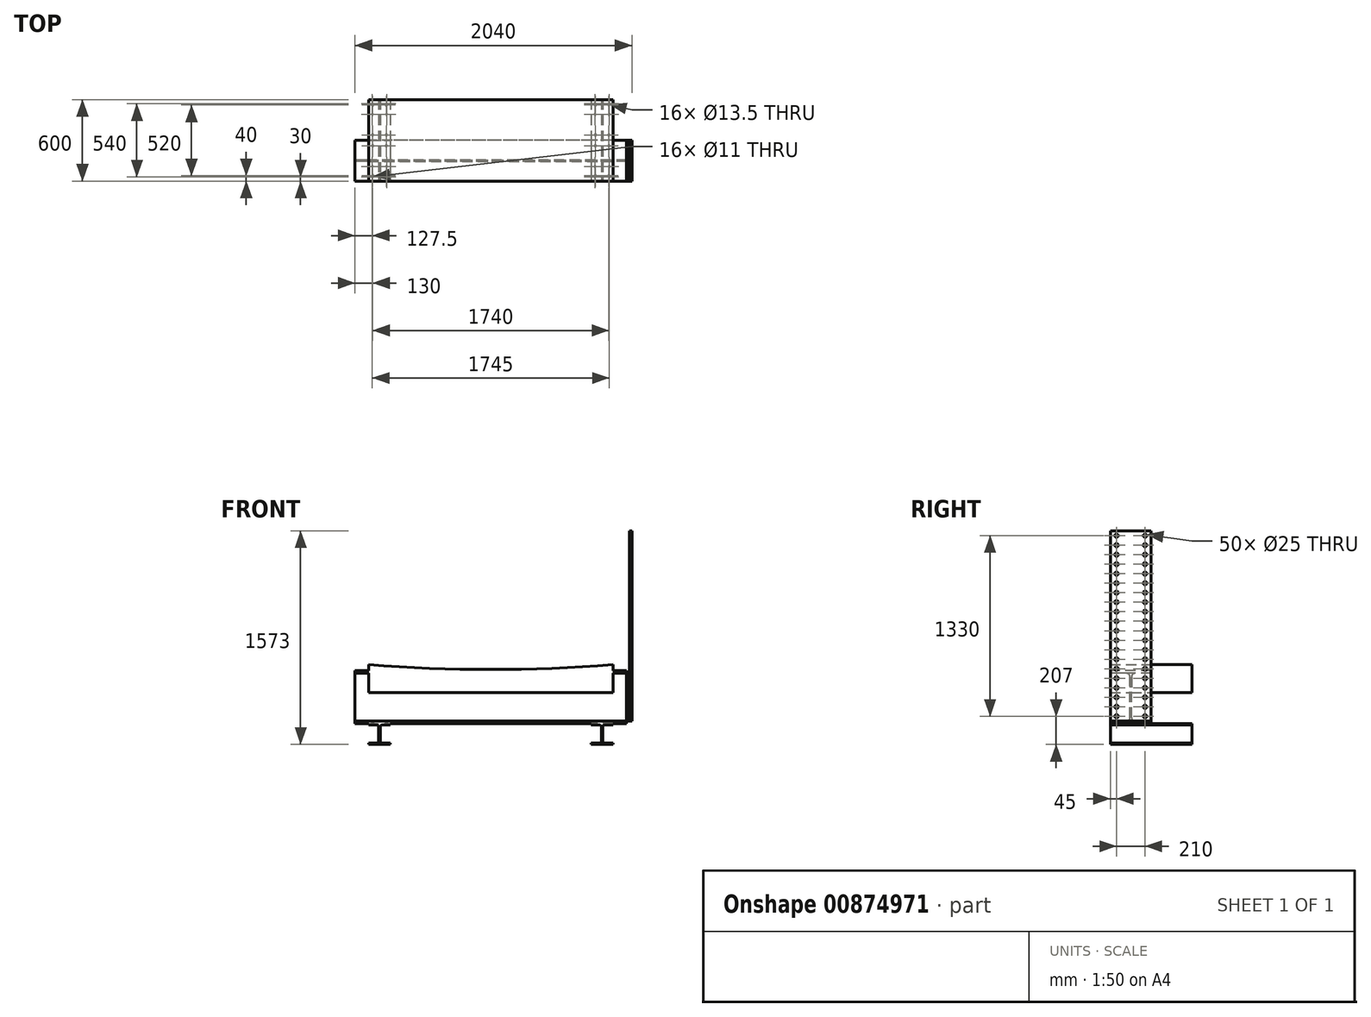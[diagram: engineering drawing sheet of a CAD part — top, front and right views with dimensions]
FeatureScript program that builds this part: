
annotation { "Feature Type Name" : "Feature", "Feature Type Description" : "" }
export const myFeature = defineFeature(function(context is Context, id is Id, definition is map)
    precondition{}
    {
        {
            var Q0;
            Q0=qCreatedBy(makeId("Front.planeOp"),FACE);
            var sketch = newSketch(context, id + "F0", { "sketchPlane" : qUnion([Q0])});
            skArc(sketch, "E0", {"start": v(-900, 40) * mm, "mid": v(0, 0) * mm, "end": v(900, 40) * mm});
            skLineSegment(sketch, "E1", {"start": v(-900, 40) * mm, "end": v(900, 40) * mm, "construction": true});
            skLineSegment(sketch, "E2", {"start": v(-900, 40) * mm, "end": v(-900, -160) * mm});
            skLineSegment(sketch, "E3", {"start": v(-900, -160) * mm, "end": v(900, -160) * mm});
            skLineSegment(sketch, "E4", {"start": v(900, -160) * mm, "end": v(900, 40) * mm});
            skSolve(sketch);
        }
        {
            var Q0;
            Q0=makeQuery(id+"F0.imprint","IMPRINT",FACE,{"disambiguationData":[TD([[makeQuery(id+"F0.imprint","IMPRINT",EDGE,{"derivedFrom":sQuery(id+"F0.wireOp",EDGE,"E0")}),-1.0]])]});
            extrude(context, id + "F1", {"entities" : qUnion([Q0]), "depth" : 300 * mm, "offsetDistance" : 25 * mm, "hasSecondDirection" : true, "secondDirectionOppositeDirection" : true, "secondDirectionDepth" : 300 * mm});
        }
        {
            var Q0;
            Q0=qCreatedBy(makeId("Front.planeOp"),FACE);
            var sketch = newSketch(context, id + "F2", { "sketchPlane" : qUnion([Q0])});
            skArc(sketch, "E5.0", {"start": v(-900, 40) * mm, "mid": v(0, 0) * mm, "end": v(900, 40) * mm});
            skLineSegment(sketch, "E6", {"start": v(-900, 40) * mm, "end": v(-900, 45) * mm});
            skLineSegment(sketch, "E7", {"start": v(900, 40) * mm, "end": v(900, 45) * mm});
            skArc(sketch, "E8", {"start": v(-900, 45) * mm, "mid": v(0, 10) * mm, "end": v(900, 45) * mm});
            skLineSegment(sketch, "E9", {"start": v(-900, 45) * mm, "end": v(900, 45) * mm, "construction": true});
            skSolve(sketch);
        }
        {
            var Q0;
            Q0 = qSketchRegion(id + "F2", true);
            extrude(context, id + "F3", {"entities" : qUnion([Q0]), "depth" : 300 * mm, "offsetDistance" : 25 * mm, "hasSecondDirection" : true, "secondDirectionOppositeDirection" : true, "secondDirectionDepth" : 300 * mm});
        }
        {
            var Q0;
            Q0=qCreatedBy(makeId("Right.planeOp"),FACE);
            var sketch = newSketch(context, id + "F4", { "sketchPlane" : qUnion([Q0])});
            skLineSegment(sketch, "E10", {"start": v(-150, 0) * mm, "end": v(0, 0) * mm});
            skLineSegment(sketch, "E11", {"start": v(0, 0) * mm, "end": v(0, -19) * mm});
            skLineSegment(sketch, "E12", {"start": v(0, -19) * mm, "end": v(-117.5, -19) * mm});
            skLineSegment(sketch, "E13", {"start": v(-144.5, -46) * mm, "end": v(-144.5, -195) * mm});
            skLineSegment(sketch, "E14", {"start": v(-144.5, -195) * mm, "end": v(-150, -195) * mm, "construction": true});
            skLineSegment(sketch, "E15", {"start": v(-150, -195) * mm, "end": v(-150, 0) * mm, "construction": true});
            skPoint(sketch, "E16.visualSharp", {"position": v(-144.5, -19) * mm});
            skArc(sketch, "E16.filletArc", {"start": v(-117.5, -19) * mm, "mid": v(-136.6, -26.9) * mm, "end": v(-144.5, -46) * mm});
            skLineSegment(sketch, "E17.MirrorCS", {"start": v(-150, 0) * mm, "end": v(-300, 0) * mm});
            skLineSegment(sketch, "E18.MirrorCS", {"start": v(-300, 0) * mm, "end": v(-300, -19) * mm});
            skLineSegment(sketch, "E19.MirrorCS", {"start": v(-300, -19) * mm, "end": v(-182.5, -19) * mm});
            skArc(sketch, "E20.MirrorCS", {"start": v(-182.5, -19) * mm, "mid": v(-163.4, -26.9) * mm, "end": v(-155.5, -46) * mm});
            skLineSegment(sketch, "E21.MirrorCS", {"start": v(-155.5, -46) * mm, "end": v(-155.5, -195) * mm});
            skLineSegment(sketch, "E22.MirrorCS", {"start": v(-144.5, -344) * mm, "end": v(-144.5, -195) * mm});
            skLineSegment(sketch, "E23.MirrorCS", {"start": v(0, -371) * mm, "end": v(-117.5, -371) * mm});
            skLineSegment(sketch, "E24.MirrorCS", {"start": v(0, -390) * mm, "end": v(0, -371) * mm});
            skLineSegment(sketch, "E25.MirrorCS", {"start": v(-150, -390) * mm, "end": v(0, -390) * mm});
            skLineSegment(sketch, "E26.MirrorCS", {"start": v(-150, -390) * mm, "end": v(-300, -390) * mm});
            skLineSegment(sketch, "E27.MirrorCS", {"start": v(-300, -390) * mm, "end": v(-300, -371) * mm});
            skLineSegment(sketch, "E28.MirrorCS", {"start": v(-300, -371) * mm, "end": v(-182.5, -371) * mm});
            skArc(sketch, "E29.MirrorCS", {"start": v(-182.5, -371) * mm, "mid": v(-163.4, -363.1) * mm, "end": v(-155.5, -344) * mm});
            skLineSegment(sketch, "E30.MirrorCS", {"start": v(-155.5, -344) * mm, "end": v(-155.5, -195) * mm});
            skArc(sketch, "E31.MirrorCS", {"start": v(-117.5, -371) * mm, "mid": v(-136.6, -363.1) * mm, "end": v(-144.5, -344) * mm});
            skSolve(sketch);
        }
        {
            var Q0;
            Q0=makeQuery(id+"F4.imprint","IMPRINT",FACE,{"disambiguationData":[TD([[makeQuery(id+"F4.imprint","IMPRINT",EDGE,{"derivedFrom":sQuery(id+"F4.wireOp",EDGE,"E10")}),-1.0]])]});
            extrude(context, id + "F5", {"entities" : qUnion([Q0]), "depth" : 1000 * mm, "offsetDistance" : 25 * mm, "hasSecondDirection" : true, "secondDirectionOppositeDirection" : true, "secondDirectionDepth" : 0 * mm});
        }
        {
            var Q0;
            Q0=makeQuery(id+"F5.opExtrude","CAP_FACE",FACE,{"disambiguationData":[OSD([sQuery(id+"F4.wireOp",EDGE,"E10"),sQuery(id+"F4.wireOp",EDGE,"E11"),sQuery(id+"F4.wireOp",EDGE,"E12"),sQuery(id+"F4.wireOp",EDGE,"E13"),sQuery(id+"F4.wireOp",EDGE,"E16.filletArc"),sQuery(id+"F4.wireOp",EDGE,"E17.MirrorCS"),sQuery(id+"F4.wireOp",EDGE,"E18.MirrorCS"),sQuery(id+"F4.wireOp",EDGE,"E19.MirrorCS"),sQuery(id+"F4.wireOp",EDGE,"E20.MirrorCS"),sQuery(id+"F4.wireOp",EDGE,"E21.MirrorCS"),sQuery(id+"F4.wireOp",EDGE,"E22.MirrorCS"),sQuery(id+"F4.wireOp",EDGE,"E23.MirrorCS"),sQuery(id+"F4.wireOp",EDGE,"E24.MirrorCS"),sQuery(id+"F4.wireOp",EDGE,"E25.MirrorCS"),sQuery(id+"F4.wireOp",EDGE,"E26.MirrorCS"),sQuery(id+"F4.wireOp",EDGE,"E27.MirrorCS"),sQuery(id+"F4.wireOp",EDGE,"E28.MirrorCS"),sQuery(id+"F4.wireOp",EDGE,"E29.MirrorCS"),sQuery(id+"F4.wireOp",EDGE,"E30.MirrorCS"),sQuery(id+"F4.wireOp",EDGE,"E31.MirrorCS")])],"isStart":false});
            var sketch = newSketch(context, id + "F6", { "sketchPlane" : qUnion([Q0])});
            skLineSegment(sketch, "E32.bottom", {"start": v(-300, -19) * mm, "end": v(0, -19) * mm});
            skLineSegment(sketch, "E32.top", {"start": v(-300, -371) * mm, "end": v(0, -371) * mm});
            skLineSegment(sketch, "E32.left", {"start": v(-300, -19) * mm, "end": v(-300, -371) * mm});
            skLineSegment(sketch, "E32.right", {"start": v(0, -19) * mm, "end": v(0, -371) * mm});
            skSolve(sketch);
        }
        {
            var Q0;
            Q0 = qSketchRegion(id + "F6", true);
            extrude(context, id + "F7", {"entities" : qUnion([Q0]), "depth" : 20 * mm, "offsetDistance" : 25 * mm});
        }
        {
            var Q0;
            Q0=makeQuery(id+"F7.opExtrude","CAP_FACE",FACE,{"disambiguationData":[OSD([sQuery(id+"F6.wireOp",EDGE,"E32.bottom"),sQuery(id+"F6.wireOp",EDGE,"E32.top"),sQuery(id+"F6.wireOp",EDGE,"E32.left"),sQuery(id+"F6.wireOp",EDGE,"E32.right")])],"isStart":false});
            var sketch = newSketch(context, id + "F8", { "sketchPlane" : qUnion([Q0])});
            skPoint(sketch, "E33", {"position": v(-255, -55) * mm});
            skPoint(sketch, "E34", {"position": v(-45, -55) * mm});
            skPoint(sketch, "E35", {"position": v(-45, -125) * mm});
            skPoint(sketch, "E36", {"position": v(-45, -195) * mm});
            skPoint(sketch, "E37", {"position": v(-45, -265) * mm});
            skPoint(sketch, "E38", {"position": v(-255, -125) * mm});
            skPoint(sketch, "E39", {"position": v(-255, -195) * mm});
            skPoint(sketch, "E40", {"position": v(-255, -265) * mm});
            skLineSegment(sketch, "E41", {"start": v(-150, -19) * mm, "end": v(-150, -371) * mm, "construction": true});
            skLineSegment(sketch, "E42", {"start": v(-255, -55) * mm, "end": v(-45, -55) * mm, "construction": true});
            skPoint(sketch, "E43", {"position": v(-150, -55) * mm});
            skLineSegment(sketch, "E44", {"start": v(-45, -55) * mm, "end": v(-45, -125) * mm, "construction": true});
            skLineSegment(sketch, "E45", {"start": v(-45, -195) * mm, "end": v(-45, -265) * mm, "construction": true});
            skLineSegment(sketch, "E46", {"start": v(-45, -195) * mm, "end": v(-45, -125) * mm, "construction": true});
            skPoint(sketch, "E47", {"position": v(-45, -335) * mm});
            skPoint(sketch, "E48", {"position": v(-255, -335) * mm});
            skLineSegment(sketch, "E49", {"start": v(-45, -265) * mm, "end": v(-45, -335) * mm, "construction": true});
            skLineSegment(sketch, "E50", {"start": v(-255, -55) * mm, "end": v(-255, -19) * mm, "construction": true});
            skLineSegment(sketch, "E51", {"start": v(-255, -335) * mm, "end": v(-255, -371) * mm, "construction": true});
            skCircle(sketch, "E52", {"center": v(-255, -55) * mm, "radius": 22 * mm, "construction": true});
            skCircle(sketch, "E53", {"center": v(-255, -125) * mm, "radius": 22 * mm, "construction": true});
            skSolve(sketch);
        }
        {
            var Q0;
            Q0=sQuery(id+"F8.wireOp",VERTEX,"E33");
            var Q1;
            Q1=sQuery(id+"F8.wireOp",VERTEX,"E34");
            var Q2;
            Q2=sQuery(id+"F8.wireOp",VERTEX,"E35");
            var Q3;
            Q3=sQuery(id+"F8.wireOp",VERTEX,"E38");
            var Q4;
            Q4=sQuery(id+"F8.wireOp",VERTEX,"E39");
            var Q5;
            Q5=sQuery(id+"F8.wireOp",VERTEX,"E36");
            var Q6;
            Q6=sQuery(id+"F8.wireOp",VERTEX,"E37");
            var Q7;
            Q7=sQuery(id+"F8.wireOp",VERTEX,"E47");
            var Q8;
            Q8=sQuery(id+"F8.wireOp",VERTEX,"E40");
            var Q9;
            Q9=sQuery(id+"F8.wireOp",VERTEX,"E48");
            var Q10;
            Q10=makeQuery(id+"F7.opExtrude","SWEPT_BODY",BODY,{"disambiguationData":[OSD([sQuery(id+"F6.wireOp",EDGE,"E32.bottom"),sQuery(id+"F6.wireOp",EDGE,"E32.top"),sQuery(id+"F6.wireOp",EDGE,"E32.left"),sQuery(id+"F6.wireOp",EDGE,"E32.right")])]});
            hole(context, id + "F9", {"style" : HoleStyle.SIMPLE, "endStyle" : HoleEndStyle.THROUGH, "holeDiameter" : 25 * mm, "majorDiameter" : 5 * mm, "isTappedThrough" : true, "tappedDepth" : 12 * mm, "tapClearance" : 3, "locations" : qUnion([Q0, Q1, Q2, Q3, Q4, Q5, Q6, Q7, Q8, Q9]), "scope" : qUnion([Q10])});
        }
        {
            var Q0;
            Q0=makeQuery(id+"F7.opExtrude","CAP_FACE",FACE,{"disambiguationData":[OSD([sQuery(id+"F6.wireOp",EDGE,"E32.bottom"),sQuery(id+"F6.wireOp",EDGE,"E32.top"),sQuery(id+"F6.wireOp",EDGE,"E32.left"),sQuery(id+"F6.wireOp",EDGE,"E32.right")])],"isStart":false});
            var sketch = newSketch(context, id + "F10", { "sketchPlane" : qUnion([Q0])});
            skLineSegment(sketch, "E54.bottom", {"start": v(-300, 1031) * mm, "end": v(0, 1031) * mm});
            skLineSegment(sketch, "E54.top", {"start": v(-300, -371) * mm, "end": v(0, -371) * mm});
            skLineSegment(sketch, "E54.left", {"start": v(-300, 1031) * mm, "end": v(-300, -371) * mm});
            skLineSegment(sketch, "E54.right", {"start": v(0, 1031) * mm, "end": v(0, -371) * mm});
            skPoint(sketch, "E55", {"position": v(-45, -335) * mm});
            skPoint(sketch, "E56", {"position": v(-255, -335) * mm});
            skPoint(sketch, "E57.0.1.0", {"position": v(-45, -265) * mm});
            skPoint(sketch, "E57.0.2.0", {"position": v(-45, -195) * mm});
            skPoint(sketch, "E57.0.3.0", {"position": v(-45, -125) * mm});
            skPoint(sketch, "E57.0.4.0", {"position": v(-45, -55) * mm});
            skPoint(sketch, "E57.0.5.0", {"position": v(-45, 15) * mm});
            skPoint(sketch, "E57.0.6.0", {"position": v(-45, 85) * mm});
            skPoint(sketch, "E57.0.7.0", {"position": v(-45, 155) * mm});
            skPoint(sketch, "E57.0.8.0", {"position": v(-45, 225) * mm});
            skPoint(sketch, "E57.0.9.0", {"position": v(-45, 295) * mm});
            skPoint(sketch, "E57.0.10.0", {"position": v(-45, 365) * mm});
            skPoint(sketch, "E57.0.11.0", {"position": v(-45, 435) * mm});
            skPoint(sketch, "E57.0.12.0", {"position": v(-45, 505) * mm});
            skPoint(sketch, "E57.0.13.0", {"position": v(-45, 575) * mm});
            skPoint(sketch, "E57.0.14.0", {"position": v(-45, 645) * mm});
            skPoint(sketch, "E57.1.1.0", {"position": v(-255, -265) * mm});
            skPoint(sketch, "E57.1.2.0", {"position": v(-255, -195) * mm});
            skPoint(sketch, "E57.1.3.0", {"position": v(-255, -125) * mm});
            skPoint(sketch, "E57.1.4.0", {"position": v(-255, -55) * mm});
            skPoint(sketch, "E57.1.5.0", {"position": v(-255, 15) * mm});
            skPoint(sketch, "E57.1.6.0", {"position": v(-255, 85) * mm});
            skPoint(sketch, "E57.1.7.0", {"position": v(-255, 155) * mm});
            skPoint(sketch, "E57.1.8.0", {"position": v(-255, 225) * mm});
            skPoint(sketch, "E57.1.9.0", {"position": v(-255, 295) * mm});
            skPoint(sketch, "E57.1.10.0", {"position": v(-255, 365) * mm});
            skPoint(sketch, "E57.1.11.0", {"position": v(-255, 435) * mm});
            skPoint(sketch, "E57.1.12.0", {"position": v(-255, 505) * mm});
            skPoint(sketch, "E57.1.13.0", {"position": v(-255, 575) * mm});
            skPoint(sketch, "E57.1.14.0", {"position": v(-255, 645) * mm});
            skLineSegment(sketch, "E57.direction1", {"start": v(-45, -335) * mm, "end": v(-255, -335) * mm, "construction": true});
            skLineSegment(sketch, "E57.direction2", {"start": v(-45, -335) * mm, "end": v(-45, -265) * mm, "construction": true});
            skPoint(sketch, "E58.0.0.15", {"position": v(-45, 715) * mm});
            skPoint(sketch, "E58.0.1.15", {"position": v(-255, 715) * mm});
            skPoint(sketch, "E59.0.0.16", {"position": v(-45, 785) * mm});
            skPoint(sketch, "E59.0.0.17", {"position": v(-45, 855) * mm});
            skPoint(sketch, "E59.0.0.18", {"position": v(-45, 925) * mm});
            skPoint(sketch, "E59.0.0.19", {"position": v(-45, 995) * mm});
            skPoint(sketch, "E59.0.1.16", {"position": v(-255, 785) * mm});
            skPoint(sketch, "E59.0.1.17", {"position": v(-255, 855) * mm});
            skPoint(sketch, "E59.0.1.18", {"position": v(-255, 925) * mm});
            skPoint(sketch, "E59.0.1.19", {"position": v(-255, 995) * mm});
            skSolve(sketch);
        }
        {
            var Q0;
            Q0 = qSketchRegion(id + "F10", true);
            extrude(context, id + "F11", {"entities" : qUnion([Q0]), "depth" : 20 * mm, "offsetDistance" : 25 * mm});
        }
        {
            var Q0;
            Q0=sQuery(id+"F10.wireOp",VERTEX,"E56");
            var Q1;
            Q1=sQuery(id+"F10.wireOp",VERTEX,"E57.1.1.0");
            var Q2;
            Q2=sQuery(id+"F10.wireOp",VERTEX,"E57.1.2.0");
            var Q3;
            Q3=sQuery(id+"F10.wireOp",VERTEX,"E57.1.3.0");
            var Q4;
            Q4=sQuery(id+"F10.wireOp",VERTEX,"E57.1.4.0");
            var Q5;
            Q5=sQuery(id+"F10.wireOp",VERTEX,"E57.1.5.0");
            var Q6;
            Q6=sQuery(id+"F10.wireOp",VERTEX,"E57.1.6.0");
            var Q7;
            Q7=sQuery(id+"F10.wireOp",VERTEX,"E57.1.7.0");
            var Q8;
            Q8=sQuery(id+"F10.wireOp",VERTEX,"E57.1.8.0");
            var Q9;
            Q9=sQuery(id+"F10.wireOp",VERTEX,"E57.1.9.0");
            var Q10;
            Q10=sQuery(id+"F10.wireOp",VERTEX,"E57.1.10.0");
            var Q11;
            Q11=sQuery(id+"F10.wireOp",VERTEX,"E57.1.11.0");
            var Q12;
            Q12=sQuery(id+"F10.wireOp",VERTEX,"E57.1.12.0");
            var Q13;
            Q13=sQuery(id+"F10.wireOp",VERTEX,"E57.1.13.0");
            var Q14;
            Q14=sQuery(id+"F10.wireOp",VERTEX,"E57.1.14.0");
            var Q15;
            Q15=sQuery(id+"F10.wireOp",VERTEX,"E58.0.1.15");
            var Q16;
            Q16=sQuery(id+"F10.wireOp",VERTEX,"E58.0.0.15");
            var Q17;
            Q17=sQuery(id+"F10.wireOp",VERTEX,"E57.0.14.0");
            var Q18;
            Q18=sQuery(id+"F10.wireOp",VERTEX,"E57.0.13.0");
            var Q19;
            Q19=sQuery(id+"F10.wireOp",VERTEX,"E57.0.12.0");
            var Q20;
            Q20=sQuery(id+"F10.wireOp",VERTEX,"E57.0.11.0");
            var Q21;
            Q21=sQuery(id+"F10.wireOp",VERTEX,"E57.0.10.0");
            var Q22;
            Q22=sQuery(id+"F10.wireOp",VERTEX,"E57.0.9.0");
            var Q23;
            Q23=sQuery(id+"F10.wireOp",VERTEX,"E57.0.8.0");
            var Q24;
            Q24=sQuery(id+"F10.wireOp",VERTEX,"E57.0.7.0");
            var Q25;
            Q25=sQuery(id+"F10.wireOp",VERTEX,"E57.0.6.0");
            var Q26;
            Q26=sQuery(id+"F10.wireOp",VERTEX,"E57.0.5.0");
            var Q27;
            Q27=sQuery(id+"F10.wireOp",VERTEX,"E57.0.4.0");
            var Q28;
            Q28=sQuery(id+"F10.wireOp",VERTEX,"E57.0.3.0");
            var Q29;
            Q29=sQuery(id+"F10.wireOp",VERTEX,"E57.0.2.0");
            var Q30;
            Q30=sQuery(id+"F10.wireOp",VERTEX,"E57.0.1.0");
            var Q31;
            Q31=sQuery(id+"F10.wireOp",VERTEX,"E55");
            var Q32;
            Q32=sQuery(id+"F10.wireOp",VERTEX,"E59.0.1.16");
            var Q33;
            Q33=sQuery(id+"F10.wireOp",VERTEX,"E59.0.0.16");
            var Q34;
            Q34=sQuery(id+"F10.wireOp",VERTEX,"E59.0.0.17");
            var Q35;
            Q35=sQuery(id+"F10.wireOp",VERTEX,"E59.0.1.17");
            var Q36;
            Q36=sQuery(id+"F10.wireOp",VERTEX,"E59.0.0.18");
            var Q37;
            Q37=sQuery(id+"F10.wireOp",VERTEX,"E59.0.0.19");
            var Q38;
            Q38=sQuery(id+"F10.wireOp",VERTEX,"E59.0.1.19");
            var Q39;
            Q39=sQuery(id+"F10.wireOp",VERTEX,"E59.0.1.20");
            var Q40;
            Q40=sQuery(id+"F10.wireOp",VERTEX,"E59.0.0.20");
            var Q41;
            Q41=sQuery(id+"F10.wireOp",VERTEX,"E59.0.0.21");
            var Q42;
            Q42=sQuery(id+"F10.wireOp",VERTEX,"E59.0.1.21");
            var Q43;
            Q43=sQuery(id+"F10.wireOp",VERTEX,"E59.0.1.22");
            var Q44;
            Q44=sQuery(id+"F10.wireOp",VERTEX,"E59.0.0.22");
            var Q45;
            Q45=sQuery(id+"F10.wireOp",VERTEX,"E59.0.0.23");
            var Q46;
            Q46=sQuery(id+"F10.wireOp",VERTEX,"E59.0.1.23");
            var Q47;
            Q47=sQuery(id+"F10.wireOp",VERTEX,"E59.0.1.24");
            var Q48;
            Q48=sQuery(id+"F10.wireOp",VERTEX,"E59.0.0.24");
            var Q49;
            Q49=sQuery(id+"F10.wireOp",VERTEX,"E59.0.1.18");
            var Q50;
            Q50=makeQuery(id+"F11.opExtrude","SWEPT_BODY",BODY,{"disambiguationData":[OSD([sQuery(id+"F10.wireOp",EDGE,"E54.bottom"),sQuery(id+"F10.wireOp",EDGE,"E54.top"),sQuery(id+"F10.wireOp",EDGE,"E54.left"),sQuery(id+"F10.wireOp",EDGE,"E54.right")])]});
            hole(context, id + "F12", {"style" : HoleStyle.SIMPLE, "endStyle" : HoleEndStyle.THROUGH, "oppositeDirection" : true, "holeDiameter" : 25 * mm, "majorDiameter" : 5 * mm, "isTappedThrough" : true, "tappedDepth" : 12 * mm, "tapClearance" : 3, "locations" : qUnion([Q0, Q1, Q2, Q3, Q4, Q5, Q6, Q7, Q8, Q9, Q10, Q11, Q12, Q13, Q14, Q15, Q16, Q17, Q18, Q19, Q20, Q21, Q22, Q23, Q24, Q25, Q26, Q27, Q28, Q29, Q30, Q31, Q32, Q33, Q34, Q35, Q36, Q37, Q38, Q39, Q40, Q41, Q42, Q43, Q44, Q45, Q46, Q47, Q48, Q49]), "scope" : qUnion([Q50])});
        }
        {
            var Q0;
            Q0=makeQuery(id+"F5.opExtrude","SWEPT_FACE",FACE,{"disambiguationData":[OSD([sQuery(id+"F4.wireOp",EDGE,"E27.MirrorCS")])]});
            var sketch = newSketch(context, id + "F13", { "sketchPlane" : qUnion([Q0])});
            skLineSegment(sketch, "E60", {"start": v(820, -466) * mm, "end": v(820, -390) * mm, "construction": true});
            skLineSegment(sketch, "E61", {"start": v(820, -390) * mm, "end": v(900, -390) * mm});
            skLineSegment(sketch, "E62", {"start": v(900, -390) * mm, "end": v(900, -399) * mm});
            skLineSegment(sketch, "E63", {"start": v(900, -399) * mm, "end": v(841, -399) * mm});
            skLineSegment(sketch, "E64", {"start": v(826, -414) * mm, "end": v(826, -466) * mm});
            skLineSegment(sketch, "E65", {"start": v(826, -466) * mm, "end": v(820, -466) * mm, "construction": true});
            skPoint(sketch, "E66.visualSharp", {"position": v(826, -399) * mm});
            skArc(sketch, "E66.filletArc", {"start": v(841, -399) * mm, "mid": v(830.4, -403.4) * mm, "end": v(826, -414) * mm});
            skLineSegment(sketch, "E67.MirrorCS", {"start": v(820, -390) * mm, "end": v(740, -390) * mm});
            skLineSegment(sketch, "E68.MirrorCS", {"start": v(740, -390) * mm, "end": v(740, -399) * mm});
            skLineSegment(sketch, "E69.MirrorCS", {"start": v(740, -399) * mm, "end": v(799, -399) * mm});
            skArc(sketch, "E70.MirrorCS", {"start": v(799, -399) * mm, "mid": v(809.6, -403.4) * mm, "end": v(814, -414) * mm});
            skLineSegment(sketch, "E71.MirrorCS", {"start": v(814, -414) * mm, "end": v(814, -466) * mm});
            skLineSegment(sketch, "E72.MirrorCS", {"start": v(826, -518) * mm, "end": v(826, -466) * mm});
            skArc(sketch, "E73.MirrorCS", {"start": v(841, -533) * mm, "mid": v(830.4, -528.6) * mm, "end": v(826, -518) * mm});
            skLineSegment(sketch, "E74.MirrorCS", {"start": v(900, -533) * mm, "end": v(841, -533) * mm});
            skLineSegment(sketch, "E75.MirrorCS", {"start": v(900, -542) * mm, "end": v(900, -533) * mm});
            skLineSegment(sketch, "E76.MirrorCS", {"start": v(820, -542) * mm, "end": v(900, -542) * mm});
            skLineSegment(sketch, "E77.MirrorCS", {"start": v(820, -542) * mm, "end": v(740, -542) * mm});
            skLineSegment(sketch, "E78.MirrorCS", {"start": v(740, -542) * mm, "end": v(740, -533) * mm});
            skLineSegment(sketch, "E79.MirrorCS", {"start": v(740, -533) * mm, "end": v(799, -533) * mm});
            skArc(sketch, "E80.MirrorCS", {"start": v(799, -533) * mm, "mid": v(809.6, -528.6) * mm, "end": v(814, -518) * mm});
            skLineSegment(sketch, "E81.MirrorCS", {"start": v(814, -518) * mm, "end": v(814, -466) * mm});
            skSolve(sketch);
        }
        {
            var Q0;
            Q0=makeQuery(id+"F13.imprint","IMPRINT",FACE,{"disambiguationData":[TD([[makeQuery(id+"F13.imprint","IMPRINT",EDGE,{"derivedFrom":sQuery(id+"F13.wireOp",EDGE,"E61")}),1.0]])]});
            var Q1;
            Q1=makeQuery(id+"F5.opExtrude","SWEPT_FACE",FACE,{"disambiguationData":[OSD([sQuery(id+"F4.wireOp",EDGE,"E24.MirrorCS")])]});
            extrude(context, id + "F14", {"entities" : qUnion([Q0]), "endBound" : BoundingType.UP_TO_SURFACE, "oppositeDirection" : true, "depth" : 25 * mm, "endBoundEntityFace" : qUnion([Q1]), "offsetDistance" : 25 * mm});
        }
        {
            var Q0;
            Q0=makeQuery(id+"F14.opExtrude","SWEPT_FACE",FACE,{"disambiguationData":[OSD([sQuery(id+"F13.wireOp",EDGE,"E63")])]});
            var sketch = newSketch(context, id + "F15", { "sketchPlane" : qUnion([Q0])});
            skLineSegment(sketch, "E82.bottom", {"start": v(770, 260) * mm, "end": v(870, 260) * mm, "construction": true});
            skLineSegment(sketch, "E82.top", {"start": v(770, 40) * mm, "end": v(870, 40) * mm, "construction": true});
            skLineSegment(sketch, "E82.left", {"start": v(770, 260) * mm, "end": v(770, 40) * mm, "construction": true});
            skLineSegment(sketch, "E82.right", {"start": v(870, 260) * mm, "end": v(870, 40) * mm, "construction": true});
            skLineSegment(sketch, "E83", {"start": v(820, 260) * mm, "end": v(820, 40) * mm, "construction": true});
            skLineSegment(sketch, "E84", {"start": v(820, 40) * mm, "end": v(820, 0) * mm});
            skSolve(sketch);
        }
        {
            var Q0;
            Q0=sQuery(id+"F15.wireOp",VERTEX,"E82.top.start");
            var Q1;
            Q1=sQuery(id+"F15.wireOp",VERTEX,"E82.top.end");
            var Q2;
            Q2=sQuery(id+"F15.wireOp",VERTEX,"E82.bottom.start");
            var Q3;
            Q3=sQuery(id+"F15.wireOp",VERTEX,"E82.bottom.end");
            var Q4;
            Q4=makeQuery(id+"F14.opExtrude","SWEPT_BODY",BODY,{"disambiguationData":[OSD([sQuery(id+"F13.wireOp",EDGE,"E61"),sQuery(id+"F13.wireOp",EDGE,"E62"),sQuery(id+"F13.wireOp",EDGE,"E63"),sQuery(id+"F13.wireOp",EDGE,"E64"),sQuery(id+"F13.wireOp",EDGE,"E66.filletArc"),sQuery(id+"F13.wireOp",EDGE,"E67.MirrorCS"),sQuery(id+"F13.wireOp",EDGE,"E68.MirrorCS"),sQuery(id+"F13.wireOp",EDGE,"E69.MirrorCS"),sQuery(id+"F13.wireOp",EDGE,"E70.MirrorCS"),sQuery(id+"F13.wireOp",EDGE,"E71.MirrorCS"),sQuery(id+"F13.wireOp",EDGE,"E72.MirrorCS"),sQuery(id+"F13.wireOp",EDGE,"E73.MirrorCS"),sQuery(id+"F13.wireOp",EDGE,"E74.MirrorCS"),sQuery(id+"F13.wireOp",EDGE,"E75.MirrorCS"),sQuery(id+"F13.wireOp",EDGE,"E76.MirrorCS"),sQuery(id+"F13.wireOp",EDGE,"E77.MirrorCS"),sQuery(id+"F13.wireOp",EDGE,"E78.MirrorCS"),sQuery(id+"F13.wireOp",EDGE,"E79.MirrorCS"),sQuery(id+"F13.wireOp",EDGE,"E80.MirrorCS"),sQuery(id+"F13.wireOp",EDGE,"E81.MirrorCS")])]});
            hole(context, id + "F16", {"style" : HoleStyle.SIMPLE, "endStyle" : HoleEndStyle.THROUGH, "standardTappedOrClearance" : lookupTablePath({ "fit" : "Normal", "standard" : "ISO", "size" : "M12", "type" : "Clearance" }), "standardBlindInLast" : lookupTablePath({ "fit" : "Normal", "standard" : "ISO", "size" : "M12", "type" : "Clearance" }), "holeDiameter" : 13.5 * mm, "majorDiameter" : 5 * mm, "isTappedThrough" : true, "tappedDepth" : 12 * mm, "tapClearance" : 3, "locations" : qUnion([Q0, Q1, Q2, Q3]), "scope" : qUnion([Q4])});
        }
        {
            var Q0;
            Q0=sQuery(id+"F15.wireOp",VERTEX,"E82.bottom.start");
            var Q1;
            Q1=sQuery(id+"F15.wireOp",VERTEX,"E82.bottom.end");
            var Q2;
            Q2=sQuery(id+"F15.wireOp",VERTEX,"E82.top.end");
            var Q3;
            Q3=sQuery(id+"F15.wireOp",VERTEX,"E82.top.start");
            var Q4;
            Q4=makeQuery(id+"F5.opExtrude","SWEPT_BODY",BODY,{"disambiguationData":[OSD([sQuery(id+"F4.wireOp",EDGE,"E10"),sQuery(id+"F4.wireOp",EDGE,"E11"),sQuery(id+"F4.wireOp",EDGE,"E12"),sQuery(id+"F4.wireOp",EDGE,"E13"),sQuery(id+"F4.wireOp",EDGE,"E16.filletArc"),sQuery(id+"F4.wireOp",EDGE,"E17.MirrorCS"),sQuery(id+"F4.wireOp",EDGE,"E18.MirrorCS"),sQuery(id+"F4.wireOp",EDGE,"E19.MirrorCS"),sQuery(id+"F4.wireOp",EDGE,"E20.MirrorCS"),sQuery(id+"F4.wireOp",EDGE,"E21.MirrorCS"),sQuery(id+"F4.wireOp",EDGE,"E22.MirrorCS"),sQuery(id+"F4.wireOp",EDGE,"E23.MirrorCS"),sQuery(id+"F4.wireOp",EDGE,"E24.MirrorCS"),sQuery(id+"F4.wireOp",EDGE,"E25.MirrorCS"),sQuery(id+"F4.wireOp",EDGE,"E26.MirrorCS"),sQuery(id+"F4.wireOp",EDGE,"E27.MirrorCS"),sQuery(id+"F4.wireOp",EDGE,"E28.MirrorCS"),sQuery(id+"F4.wireOp",EDGE,"E29.MirrorCS"),sQuery(id+"F4.wireOp",EDGE,"E30.MirrorCS"),sQuery(id+"F4.wireOp",EDGE,"E31.MirrorCS")])]});
            hole(context, id + "F17", {"style" : HoleStyle.SIMPLE, "endStyle" : HoleEndStyle.BLIND, "standardTappedOrClearance" : lookupTablePath({ "fit" : "Normal", "standard" : "ISO", "size" : "M12", "type" : "Clearance" }), "standardBlindInLast" : lookupTablePath({ "fit" : "Normal", "standard" : "ISO", "size" : "M12", "type" : "Clearance" }), "holeDiameter" : 13.5 * mm, "majorDiameter" : 12 * mm, "holeDepth" : 30 * mm, "isTappedThrough" : true, "tappedDepth" : 12 * mm, "tapClearance" : 3, "locations" : qUnion([Q0, Q1, Q2, Q3]), "scope" : qUnion([Q4])});
        }
        {
            var Q0;
            Q0=makeQuery(id+"F14.opExtrude","SWEPT_FACE",FACE,{"disambiguationData":[OSD([sQuery(id+"F13.wireOp",EDGE,"E76.MirrorCS"),sQuery(id+"F13.wireOp",EDGE,"E77.MirrorCS")])]});
            var sketch = newSketch(context, id + "F18", { "sketchPlane" : qUnion([Q0])});
            skLineSegment(sketch, "E85.bottom", {"start": v(767.5, 270) * mm, "end": v(872.5, 270) * mm});
            skLineSegment(sketch, "E85.top", {"start": v(767.5, 192.5) * mm, "end": v(872.5, 192.5) * mm});
            skLineSegment(sketch, "E85.left", {"start": v(767.5, 270) * mm, "end": v(767.5, 192.5) * mm});
            skLineSegment(sketch, "E85.right", {"start": v(872.5, 270) * mm, "end": v(872.5, 192.5) * mm});
            skLineSegment(sketch, "E86", {"start": v(820, 192.5) * mm, "end": v(820, 270) * mm, "construction": true});
            skLineSegment(sketch, "E87", {"start": v(820, 270) * mm, "end": v(820, 300) * mm, "construction": true});
            skSolve(sketch);
        }
        {
            var Q0;
            Q0=sQuery(id+"F18.wireOp",VERTEX,"E85.bottom.start");
            var Q1;
            Q1=sQuery(id+"F18.wireOp",VERTEX,"E85.bottom.end");
            var Q2;
            Q2=sQuery(id+"F18.wireOp",VERTEX,"E85.top.end");
            var Q3;
            Q3=sQuery(id+"F18.wireOp",VERTEX,"E85.top.start");
            var Q4;
            Q4=makeQuery(id+"F14.opExtrude","SWEPT_BODY",BODY,{"disambiguationData":[OSD([sQuery(id+"F13.wireOp",EDGE,"E61"),sQuery(id+"F13.wireOp",EDGE,"E62"),sQuery(id+"F13.wireOp",EDGE,"E63"),sQuery(id+"F13.wireOp",EDGE,"E64"),sQuery(id+"F13.wireOp",EDGE,"E66.filletArc"),sQuery(id+"F13.wireOp",EDGE,"E67.MirrorCS"),sQuery(id+"F13.wireOp",EDGE,"E68.MirrorCS"),sQuery(id+"F13.wireOp",EDGE,"E69.MirrorCS"),sQuery(id+"F13.wireOp",EDGE,"E70.MirrorCS"),sQuery(id+"F13.wireOp",EDGE,"E71.MirrorCS"),sQuery(id+"F13.wireOp",EDGE,"E72.MirrorCS"),sQuery(id+"F13.wireOp",EDGE,"E73.MirrorCS"),sQuery(id+"F13.wireOp",EDGE,"E74.MirrorCS"),sQuery(id+"F13.wireOp",EDGE,"E75.MirrorCS"),sQuery(id+"F13.wireOp",EDGE,"E76.MirrorCS"),sQuery(id+"F13.wireOp",EDGE,"E77.MirrorCS"),sQuery(id+"F13.wireOp",EDGE,"E78.MirrorCS"),sQuery(id+"F13.wireOp",EDGE,"E79.MirrorCS"),sQuery(id+"F13.wireOp",EDGE,"E80.MirrorCS"),sQuery(id+"F13.wireOp",EDGE,"E81.MirrorCS")])]});
            hole(context, id + "F19", {"style" : HoleStyle.SIMPLE, "endStyle" : HoleEndStyle.BLIND, "standardTappedOrClearance" : lookupTablePath({ "fit" : "Normal", "standard" : "ISO", "size" : "M10", "type" : "Clearance" }), "standardBlindInLast" : lookupTablePath({ "fit" : "Normal", "standard" : "ISO", "size" : "M10", "type" : "Clearance" }), "holeDiameter" : 11 * mm, "majorDiameter" : 5 * mm, "holeDepth" : 30 * mm, "isTappedThrough" : true, "tappedDepth" : 12 * mm, "tapClearance" : 3, "locations" : qUnion([Q0, Q1, Q2, Q3]), "scope" : qUnion([Q4])});
        }
        {
            var Q0;
            Q0=makeQuery(id+"F14.opExtrude","SWEPT_BODY",BODY,{"disambiguationData":[OSD([sQuery(id+"F13.wireOp",EDGE,"E61"),sQuery(id+"F13.wireOp",EDGE,"E62"),sQuery(id+"F13.wireOp",EDGE,"E63"),sQuery(id+"F13.wireOp",EDGE,"E64"),sQuery(id+"F13.wireOp",EDGE,"E66.filletArc"),sQuery(id+"F13.wireOp",EDGE,"E67.MirrorCS"),sQuery(id+"F13.wireOp",EDGE,"E68.MirrorCS"),sQuery(id+"F13.wireOp",EDGE,"E69.MirrorCS"),sQuery(id+"F13.wireOp",EDGE,"E70.MirrorCS"),sQuery(id+"F13.wireOp",EDGE,"E71.MirrorCS"),sQuery(id+"F13.wireOp",EDGE,"E72.MirrorCS"),sQuery(id+"F13.wireOp",EDGE,"E73.MirrorCS"),sQuery(id+"F13.wireOp",EDGE,"E74.MirrorCS"),sQuery(id+"F13.wireOp",EDGE,"E75.MirrorCS"),sQuery(id+"F13.wireOp",EDGE,"E76.MirrorCS"),sQuery(id+"F13.wireOp",EDGE,"E77.MirrorCS"),sQuery(id+"F13.wireOp",EDGE,"E78.MirrorCS"),sQuery(id+"F13.wireOp",EDGE,"E79.MirrorCS"),sQuery(id+"F13.wireOp",EDGE,"E80.MirrorCS"),sQuery(id+"F13.wireOp",EDGE,"E81.MirrorCS")])]});
            var Q1;
            Q1=makeQuery(id+"F14.opExtrude","CAP_FACE",FACE,{"disambiguationData":[OSD([sQuery(id+"F13.wireOp",EDGE,"E61"),sQuery(id+"F13.wireOp",EDGE,"E62"),sQuery(id+"F13.wireOp",EDGE,"E63"),sQuery(id+"F13.wireOp",EDGE,"E64"),sQuery(id+"F13.wireOp",EDGE,"E66.filletArc"),sQuery(id+"F13.wireOp",EDGE,"E67.MirrorCS"),sQuery(id+"F13.wireOp",EDGE,"E68.MirrorCS"),sQuery(id+"F13.wireOp",EDGE,"E69.MirrorCS"),sQuery(id+"F13.wireOp",EDGE,"E70.MirrorCS"),sQuery(id+"F13.wireOp",EDGE,"E71.MirrorCS"),sQuery(id+"F13.wireOp",EDGE,"E72.MirrorCS"),sQuery(id+"F13.wireOp",EDGE,"E73.MirrorCS"),sQuery(id+"F13.wireOp",EDGE,"E74.MirrorCS"),sQuery(id+"F13.wireOp",EDGE,"E75.MirrorCS"),sQuery(id+"F13.wireOp",EDGE,"E76.MirrorCS"),sQuery(id+"F13.wireOp",EDGE,"E77.MirrorCS"),sQuery(id+"F13.wireOp",EDGE,"E78.MirrorCS"),sQuery(id+"F13.wireOp",EDGE,"E79.MirrorCS"),sQuery(id+"F13.wireOp",EDGE,"E80.MirrorCS"),sQuery(id+"F13.wireOp",EDGE,"E81.MirrorCS")])],"isStart":false});
            mirror(context, id + "F20", {"operationType" : NewBodyOperationType.ADD, "entities" : qUnion([Q0]), "mirrorPlane" : qUnion([Q1])});
        }
        {
            var Q0;
            Q0=makeQuery(id+"F5.opExtrude","SWEPT_BODY",BODY,{"disambiguationData":[OSD([sQuery(id+"F4.wireOp",EDGE,"E10"),sQuery(id+"F4.wireOp",EDGE,"E11"),sQuery(id+"F4.wireOp",EDGE,"E12"),sQuery(id+"F4.wireOp",EDGE,"E13"),sQuery(id+"F4.wireOp",EDGE,"E16.filletArc"),sQuery(id+"F4.wireOp",EDGE,"E17.MirrorCS"),sQuery(id+"F4.wireOp",EDGE,"E18.MirrorCS"),sQuery(id+"F4.wireOp",EDGE,"E19.MirrorCS"),sQuery(id+"F4.wireOp",EDGE,"E20.MirrorCS"),sQuery(id+"F4.wireOp",EDGE,"E21.MirrorCS"),sQuery(id+"F4.wireOp",EDGE,"E22.MirrorCS"),sQuery(id+"F4.wireOp",EDGE,"E23.MirrorCS"),sQuery(id+"F4.wireOp",EDGE,"E24.MirrorCS"),sQuery(id+"F4.wireOp",EDGE,"E25.MirrorCS"),sQuery(id+"F4.wireOp",EDGE,"E26.MirrorCS"),sQuery(id+"F4.wireOp",EDGE,"E27.MirrorCS"),sQuery(id+"F4.wireOp",EDGE,"E28.MirrorCS"),sQuery(id+"F4.wireOp",EDGE,"E29.MirrorCS"),sQuery(id+"F4.wireOp",EDGE,"E30.MirrorCS"),sQuery(id+"F4.wireOp",EDGE,"E31.MirrorCS")])]});
            var Q1;
            Q1=makeQuery(id+"F5.opExtrude","CAP_FACE",FACE,{"disambiguationData":[OSD([sQuery(id+"F4.wireOp",EDGE,"E10"),sQuery(id+"F4.wireOp",EDGE,"E11"),sQuery(id+"F4.wireOp",EDGE,"E12"),sQuery(id+"F4.wireOp",EDGE,"E13"),sQuery(id+"F4.wireOp",EDGE,"E16.filletArc"),sQuery(id+"F4.wireOp",EDGE,"E17.MirrorCS"),sQuery(id+"F4.wireOp",EDGE,"E18.MirrorCS"),sQuery(id+"F4.wireOp",EDGE,"E19.MirrorCS"),sQuery(id+"F4.wireOp",EDGE,"E20.MirrorCS"),sQuery(id+"F4.wireOp",EDGE,"E21.MirrorCS"),sQuery(id+"F4.wireOp",EDGE,"E22.MirrorCS"),sQuery(id+"F4.wireOp",EDGE,"E23.MirrorCS"),sQuery(id+"F4.wireOp",EDGE,"E24.MirrorCS"),sQuery(id+"F4.wireOp",EDGE,"E25.MirrorCS"),sQuery(id+"F4.wireOp",EDGE,"E26.MirrorCS"),sQuery(id+"F4.wireOp",EDGE,"E27.MirrorCS"),sQuery(id+"F4.wireOp",EDGE,"E28.MirrorCS"),sQuery(id+"F4.wireOp",EDGE,"E29.MirrorCS"),sQuery(id+"F4.wireOp",EDGE,"E30.MirrorCS"),sQuery(id+"F4.wireOp",EDGE,"E31.MirrorCS")])],"isStart":true});
            mirror(context, id + "F21", {"operationType" : NewBodyOperationType.ADD, "entities" : qUnion([Q0]), "mirrorPlane" : qUnion([Q1])});
        }
    });
